# Revit family: Shower-Receptor-Sterling-Guard-72321100
name_source: partatom
category: Plumbing Fixtures
revit_build: Autodesk Revit 2015 (Build: 20140606_1530(x64)
units: mm (PartAtom-declared; Revit-internal decimal feet)

## types (2) — shared parameters
ADA Compliant = Yes
Assembly Code = C1030200
Date Modified = 09/18/2017
Default Elevation = 0"
Description = GUARD+™48 inch Shower Base
Flow Rate = 0 GPM
Height = 4 3/16"
Inlet Connection = Inlet Connection
Length = 48"
Manufacturer = Sterling
MasterFormat 1995 = 15410
MasterFormat 2004 = 22.41.23
Material = Vikrell® material
Outlet Connection = Outlet Connection
Pressure = 0.00 psi
Product Documentation Link = https://www.sterlingplumbing.com
Product Name = GUARD+
Product Page URL = http://www.sterlingplumbing.com
URL = https://www.sterlingplumbing.com
Waste Connection = Yes
Width = 34"

## per-type parameters (varying)
| type | Finish | Model | Type |
| 48"-0-White | Vitreous China - Kohler - 0 - White | 72321100-0-White | 1 |
| 48"-96-Biscuit | Vitreous China - Kohler - 96 - Biscuit | 72321100-96-Biscuit | 2 |

## geometry (parser evidence)
native form markers: Sweep x7
no freeform markers — native parametric forms only
